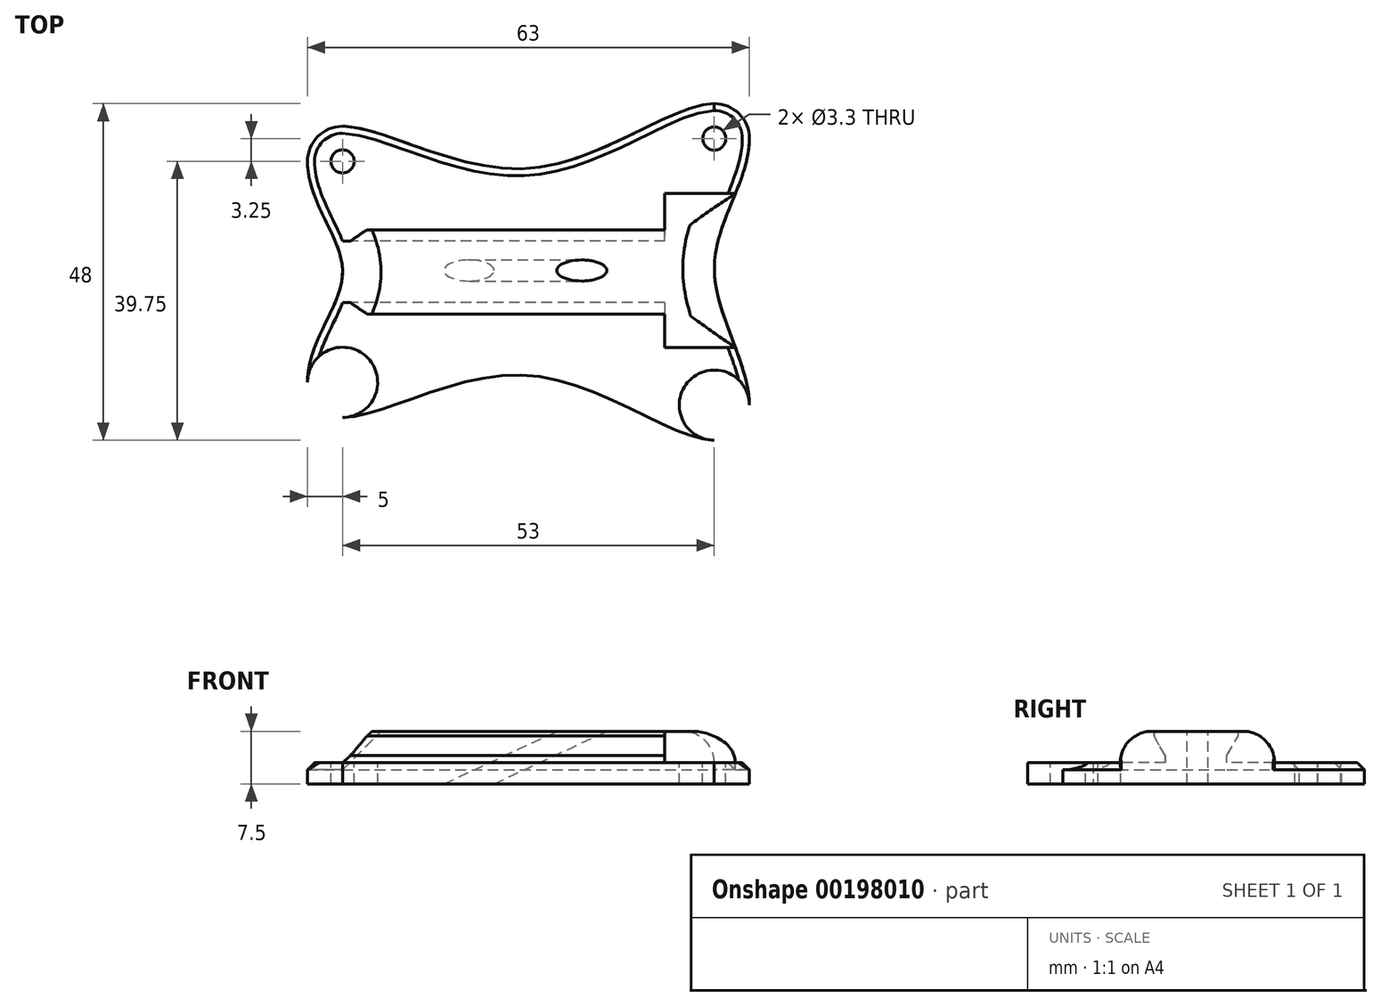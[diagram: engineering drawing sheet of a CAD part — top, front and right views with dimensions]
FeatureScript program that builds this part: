
annotation { "Feature Type Name" : "Feature", "Feature Type Description" : "" }
export const myFeature = defineFeature(function(context is Context, id is Id, definition is map)
    precondition{}
    {
        {
            var Q0;
            Q0=qCreatedBy(makeId("Top.planeOp"),FACE);
            var sketch = newSketch(context, id + "F0", { "sketchPlane" : qUnion([Q0])});
            skCircle(sketch, "E0", {"center": v(-26.5, 15.75) * mm, "radius": 5 * mm});
            skCircle(sketch, "E1", {"center": v(26.5, 19) * mm, "radius": 5 * mm});
            skFitSpline(sketch, "E2", {"points": [v(-26.5, 20.75) * mm, v(0, 14.75) * mm, v(26.5, 24) * mm], "startDerivative": vector(36.3, 0) * mm, "endDerivative": vector(35.7, 0) * mm});
            skCircle(sketch, "E3.MirrorC", {"center": v(-26.5, -15.75) * mm, "radius": 5 * mm});
            skCircle(sketch, "E4.MirrorC", {"center": v(26.5, -19) * mm, "radius": 5 * mm});
            skFitSpline(sketch, "E5", {"points": [v(-31.5, 15.75) * mm, v(-26.5, 0) * mm, v(-31.5, -15.75) * mm], "startDerivative": vector(0, -36) * mm, "endDerivative": vector(0, -36) * mm});
            skFitSpline(sketch, "E6", {"points": [v(31.5, 19) * mm, v(26.5, 0.68) * mm, v(31.5, -19) * mm], "startDerivative": vector(0, -36.61) * mm, "endDerivative": vector(0, -35.4) * mm});
            skFitSpline(sketch, "E7.MirrorCS", {"points": [v(-26.5, -20.75) * mm, v(0, -14.75) * mm, v(26.5, -24) * mm], "startDerivative": vector(36.3, 0) * mm, "endDerivative": vector(35.7, 0) * mm});
            skLineSegment(sketch, "E8", {"start": v(-31.5, 15.75) * mm, "end": v(-31.5, -15.75) * mm});
            skLineSegment(sketch, "E9", {"start": v(31.5, -19) * mm, "end": v(31.5, 19) * mm});
            skSolve(sketch);
        }
        {
            var Q0;
            {var subQ0=sQuery(id+"F0.wireOp",EDGE,"E0");var subQ1=makeQuery(id+"F0.imprint","INTERSECT",VERTEX,{"derivedFrom":[subQ0,sQuery(id+"F0.wireOp",EDGE,"E2")]});Q0=makeQuery(id+"F0.imprint","IMPRINT",FACE,{"disambiguationData":[TD([[makeQuery(id+"F0.imprint","IMPRINT",EDGE,{"disambiguationData":[TD([[subQ1,-1.0]])],"derivedFrom":subQ0}),1.0]])]});}
            var Q1;
            {var subQ3=sQuery(id+"F0.wireOp",EDGE,"E2");Q1=makeQuery(id+"F0.imprint","IMPRINT",FACE,{"disambiguationData":[TD([[makeQuery(id+"F0.imprint","IMPRINT",EDGE,{"derivedFrom":subQ3}),-1.0]])]});}
            var Q2;
            {var subQ0=sQuery(id+"F0.wireOp",EDGE,"E1");var subQ1=makeQuery(id+"F0.imprint","INTERSECT",VERTEX,{"derivedFrom":[subQ0,sQuery(id+"F0.wireOp",EDGE,"E2")]});Q2=makeQuery(id+"F0.imprint","IMPRINT",FACE,{"disambiguationData":[TD([[makeQuery(id+"F0.imprint","IMPRINT",EDGE,{"disambiguationData":[TD([[subQ1,-1.0]])],"derivedFrom":subQ0}),1.0]])]});}
            var Q3;
            {var subQ0=sQuery(id+"F0.wireOp",EDGE,"E4.MirrorC");var subQ1=makeQuery(id+"F0.imprint","INTERSECT",VERTEX,{"derivedFrom":[sQuery(id+"F0.wireOp",EDGE,"a44881bb-c97c-418e-afc0-beb98dd81ed20.MirrorCS"),subQ0]});Q3=makeQuery(id+"F0.imprint","IMPRINT",FACE,{"disambiguationData":[TD([[makeQuery(id+"F0.imprint","IMPRINT",EDGE,{"disambiguationData":[TD([[subQ1,-1.0]])],"derivedFrom":subQ0}),-1.0]])]});}
            var Q4;
            {var subQ0=sQuery(id+"F0.wireOp",EDGE,"E3.MirrorC");var subQ1=makeQuery(id+"F0.imprint","INTERSECT",VERTEX,{"derivedFrom":[subQ0,sQuery(id+"F0.wireOp",EDGE,"a44881bb-c97c-418e-afc0-beb98dd81ed20.MirrorCS")]});Q4=makeQuery(id+"F0.imprint","IMPRINT",FACE,{"disambiguationData":[TD([[makeQuery(id+"F0.imprint","IMPRINT",EDGE,{"disambiguationData":[TD([[subQ1,-1.0]])],"derivedFrom":subQ0}),-1.0]])]});}
            extrude(context, id + "F1", {"entities" : qUnion([Q0, Q1, Q2, Q3, Q4]), "oppositeDirection" : true, "depth" : 3 * mm});
        }
        {
            var Q0;
            Q0=sQuery(id+"F0.wireOp",VERTEX,"E0.center");
            var Q1;
            Q1=sQuery(id+"F0.wireOp",VERTEX,"E3.MirrorC.center");
            var Q2;
            Q2=sQuery(id+"F0.wireOp",VERTEX,"E1.center");
            var Q3;
            Q3=sQuery(id+"F0.wireOp",VERTEX,"E4.MirrorC.center");
            var Q4;
            Q4=makeQuery(id+"F1.opExtrude","SWEPT_BODY",BODY,{"disambiguationData":[OSD([sQuery(id+"F0.wireOp",EDGE,"E0"),sQuery(id+"F0.wireOp",EDGE,"E1"),sQuery(id+"F0.wireOp",EDGE,"E2"),sQuery(id+"F0.wireOp",EDGE,"E3.MirrorC"),sQuery(id+"F0.wireOp",EDGE,"E4.MirrorC"),sQuery(id+"F0.wireOp",EDGE,"E5"),sQuery(id+"F0.wireOp",EDGE,"E6"),sQuery(id+"F0.wireOp",EDGE,"E7.MirrorCS")])]});
            hole(context, id + "F2", {"style" : HoleStyle.SIMPLE, "endStyle" : HoleEndStyle.THROUGH, "holeDiameter" : 3.3 * mm, "locations" : qUnion([Q0, Q1, Q2, Q3]), "scope" : qUnion([Q4]), "isTappedThrough" : true});
        }
        {
            var Q0;
            Q0=sQuery(id+"F0.wireOp",EDGE,"E8");
            var Q1;
            {var subQ3=sQuery(id+"F0.wireOp",EDGE,"E2");Q1=makeQuery(id+"F0.imprint","IMPRINT",FACE,{"disambiguationData":[TD([[makeQuery(id+"F0.imprint","IMPRINT",EDGE,{"derivedFrom":subQ3}),-1.0]])]});}
            cPlane(context, id + "F3", {"entities" : qUnion([Q0, Q1]), "cplaneType" : CPlaneType.LINE_ANGLE, "offset" : 25 * mm, "angle" : 90 * degree, "width" : 150 * mm, "height" : 150 * mm});
        }
        {
            var Q0;
            Q0=qCreatedBy(id+"F3.planeOp",FACE);
            var sketch = newSketch(context, id + "F4", { "sketchPlane" : qUnion([Q0])});
            skLineSegment(sketch, "E10.bottom", {"start": v(6.4, 4.5) * mm, "end": v(-6.4, 4.5) * mm});
            skLineSegment(sketch, "E10.top", {"start": v(6.4, 0) * mm, "end": v(-6.4, 0) * mm});
            skLineSegment(sketch, "E10.left", {"start": v(6.4, 4.5) * mm, "end": v(6.4, 0) * mm});
            skLineSegment(sketch, "E10.right", {"start": v(-6.4, 4.5) * mm, "end": v(-6.4, 0) * mm});
            skLineSegment(sketch, "E11", {"start": v(6.4, 4.5) * mm, "end": v(4.4, 1.04) * mm});
            skLineSegment(sketch, "E12", {"start": v(4.4, 1.04) * mm, "end": v(4.4, 0) * mm});
            skLineSegment(sketch, "E13", {"start": v(0, 4.5) * mm, "end": v(0, 0) * mm, "construction": true});
            skLineSegment(sketch, "E14.MirrorCS", {"start": v(-6.4, 4.5) * mm, "end": v(-4.4, 1.04) * mm});
            skLineSegment(sketch, "E15.MirrorCS", {"start": v(-4.4, 1.04) * mm, "end": v(-4.4, 0) * mm});
            skLineSegment(sketch, "E16", {"start": v(6, 4.5) * mm, "end": v(6, 3.8) * mm});
            skLineSegment(sketch, "E17.MirrorCS", {"start": v(-6, 4.5) * mm, "end": v(-6, 3.8) * mm});
            skSolve(sketch);
        }
        {
            var Q0;
            {var subQ0=sQuery(id+"F4.wireOp",EDGE,"E12");Q0=makeQuery(id+"F4.imprint","IMPRINT",FACE,{"disambiguationData":[TD([[makeQuery(id+"F4.imprint","IMPRINT",EDGE,{"derivedFrom":subQ0}),-1.0]])]});}
            var Q1;
            Q1=makeQuery(id+"F1.opExtrude","SWEPT_BODY",BODY,{"disambiguationData":[OSD([sQuery(id+"F0.wireOp",EDGE,"E0"),sQuery(id+"F0.wireOp",EDGE,"E1"),sQuery(id+"F0.wireOp",EDGE,"E2"),sQuery(id+"F0.wireOp",EDGE,"E3.MirrorC"),sQuery(id+"F0.wireOp",EDGE,"E4.MirrorC"),sQuery(id+"F0.wireOp",EDGE,"E5"),sQuery(id+"F0.wireOp",EDGE,"E6"),sQuery(id+"F0.wireOp",EDGE,"E7.MirrorCS")])]});
            extrude(context, id + "F5", {"entities" : qUnion([Q0]), "operationType" : NewBodyOperationType.ADD, "endBoundEntityBody" : qUnion([Q1]), "depth" : 60.95 * mm});
        }
        {
            var Q0;
            Q0=makeQuery(id+"F5.opExtrude","SWEPT_FACE",FACE,{"disambiguationData":[OSD([sQuery(id+"F4.wireOp",EDGE,"E10.bottom")])]});
            var sketch = newSketch(context, id + "F6", { "sketchPlane" : qUnion([Q0])});
            skLineSegment(sketch, "E18.bottom", {"start": v(19.45, 11.2) * mm, "end": v(29.45, 11.2) * mm});
            skLineSegment(sketch, "E18.top", {"start": v(19.45, -10.8) * mm, "end": v(29.45, -10.8) * mm});
            skLineSegment(sketch, "E18.left", {"start": v(19.45, 11.2) * mm, "end": v(19.45, -10.8) * mm});
            skLineSegment(sketch, "E18.right", {"start": v(29.45, 11.2) * mm, "end": v(29.45, -10.8) * mm});
            skSolve(sketch);
        }
        {
            var Q0;
            Q0=sQuery(id+"F6.wireOp",EDGE,"E18.left");
            var Q1;
            {var subQ1=sQuery(id+"F4.wireOp",EDGE,"E10.bottom");var subQ6=makeQuery(id+"F5.opExtrude","CAP_EDGE",EDGE,{"disambiguationData":[OSD([subQ1])],"isStart":true});Q1=makeQuery(id+"F6.imprint","IMPRINT",FACE,{"disambiguationData":[TD([[makeQuery(id+"F6.imprint","IMPRINT",EDGE,{"derivedFrom":subQ6}),1.0]])]});}
            cPlane(context, id + "F7", {"entities" : qUnion([Q0, Q1]), "cplaneType" : CPlaneType.LINE_ANGLE, "offset" : 25 * mm, "angle" : 115 * degree, "width" : 150 * mm, "height" : 150 * mm});
        }
        {
            var Q0;
            {var subQ0=sQuery(id+"F6.wireOp",EDGE,"E18.top");Q0=makeQuery(id+"F6.imprint","IMPRINT",FACE,{"disambiguationData":[TD([[makeQuery(id+"F6.imprint","IMPRINT",EDGE,{"derivedFrom":subQ0}),1.0]])]});}
            var Q1;
            {var subQ0=sQuery(id+"F6.wireOp",EDGE,"E18.left");var subQ1=sQuery(id+"F4.wireOp",EDGE,"E10.bottom");var subQ2=makeQuery(id+"F5.opExtrude","SWEPT_EDGE",EDGE,{"disambiguationData":[OSD([subQ1,sQuery(id+"F4.wireOp",EDGE,"E10.left"),sQuery(id+"F4.wireOp",EDGE,"E11")])]});var subQ3=makeQuery(id+"F6.imprint","INTERSECT",VERTEX,{"derivedFrom":[subQ2,subQ0]});Q1=makeQuery(id+"F6.imprint","IMPRINT",FACE,{"disambiguationData":[TD([[makeQuery(id+"F6.imprint","IMPRINT",EDGE,{"disambiguationData":[TD([[subQ3,-1.0]])],"derivedFrom":subQ0}),1.0]])]});}
            var Q2;
            {var subQ0=sQuery(id+"F6.wireOp",EDGE,"E18.bottom");Q2=makeQuery(id+"F6.imprint","IMPRINT",FACE,{"disambiguationData":[TD([[makeQuery(id+"F6.imprint","IMPRINT",EDGE,{"derivedFrom":subQ0}),-1.0]])]});}
            extrude(context, id + "F8", {"entities" : qUnion([Q0, Q1, Q2]), "operationType" : NewBodyOperationType.ADD, "oppositeDirection" : true, "depth" : 4.5 * mm});
        }
        {
            var Q0;
            Q0=makeQuery(id+"F0.imprint","IMPRINT",FACE,{"disambiguationData":[TD([[makeQuery(id+"F0.imprint","IMPRINT",EDGE,{"derivedFrom":sQuery(id+"F0.wireOp",EDGE,"E6")}),1.0]])]});
            var Q1;
            Q1=makeQuery(id+"F0.imprint","IMPRINT",FACE,{"disambiguationData":[TD([[makeQuery(id+"F0.imprint","IMPRINT",EDGE,{"derivedFrom":sQuery(id+"F0.wireOp",EDGE,"E5")}),-1.0]])]});
            extrude(context, id + "F9", {"entities" : qUnion([Q0, Q1]), "operationType" : NewBodyOperationType.REMOVE, "endBound" : BoundingType.THROUGH_ALL, "depth" : 25 * mm});
        }
        {
            var Q0;
            Q0=makeQuery(id+"F8.opExtrude","CAP_EDGE",EDGE,{"disambiguationData":[OSD([sQuery(id+"F6.wireOp",EDGE,"E18.top")])],"isStart":true});
            var Q1;
            Q1=makeQuery(id+"F9.boolean.opBoolean","INTERSECT",EDGE,{"derivedFrom":[makeQuery(id+"F8.boolean.opBoolean","MERGE",FACE,{"derivedFrom":[makeQuery(id+"F5.opExtrude","SWEPT_FACE",FACE,{"disambiguationData":[OSD([sQuery(id+"F4.wireOp",EDGE,"E10.bottom")])]}),makeQuery(id+"F8.opExtrude","CAP_FACE",FACE,{"disambiguationData":[OSD([sQuery(id+"F6.wireOp",EDGE,"E18.bottom"),sQuery(id+"F6.wireOp",EDGE,"E18.top"),sQuery(id+"F6.wireOp",EDGE,"E18.left"),sQuery(id+"F6.wireOp",EDGE,"E18.right")])],"isStart":true})]}),makeQuery(id+"F9.opExtrude","SWEPT_FACE",FACE,{"disambiguationData":[OSD([sQuery(id+"F0.wireOp",EDGE,"E6")])]})]});
            var Q2;
            Q2=makeQuery(id+"F8.opExtrude","CAP_EDGE",EDGE,{"disambiguationData":[OSD([sQuery(id+"F6.wireOp",EDGE,"E18.bottom")])],"isStart":true});
            fillet(context, id + "F10", {"entities" : qUnion([Q0, Q1, Q2]), "radius" : 4.5 * mm, "tangentPropagation" : true, "allowEdgeOverflow" : false});
        }
        {
            var Q0;
            {var subQ0=sQuery(id+"F0.wireOp",EDGE,"E6");var subQ1=sQuery(id+"F0.wireOp",EDGE,"E1");Q0=makeQuery(id+"F8.boolean.opBoolean","SPLIT",EDGE,{"derivedFrom":makeQuery(id+"F5.boolean.opBoolean","SPLIT",EDGE,{"disambiguationData":[TD([makeQuery(id+"F1.opExtrude","CAP_FACE",FACE,{"disambiguationData":[OSD([sQuery(id+"F0.wireOp",EDGE,"E0"),subQ1,sQuery(id+"F0.wireOp",EDGE,"E2"),sQuery(id+"F0.wireOp",EDGE,"E3.MirrorC"),sQuery(id+"F0.wireOp",EDGE,"E4.MirrorC"),sQuery(id+"F0.wireOp",EDGE,"E5"),subQ0,sQuery(id+"F0.wireOp",EDGE,"E7.MirrorCS")])],"isStart":true}),makeQuery(id+"F1.opExtrude","SWEPT_FACE",FACE,{"disambiguationData":[OSD([subQ1])]}),makeQuery(id+"F1.opExtrude","SWEPT_FACE",FACE,{"disambiguationData":[OSD([subQ0])]}),makeQuery(id+"F5.opExtrude","SWEPT_FACE",FACE,{"disambiguationData":[OSD([sQuery(id+"F4.wireOp",EDGE,"E10.top")])]}),makeQuery(id+"F5.opExtrude","SWEPT_FACE",FACE,{"disambiguationData":[OSD([sQuery(id+"F4.wireOp",EDGE,"E12")])]})])],"derivedFrom":makeQuery(id+"F1.opExtrude","CAP_EDGE",EDGE,{"disambiguationData":[OSD([subQ0])],"isStart":true})})});}
            var Q1;
            {var subQ0=sQuery(id+"F0.wireOp",EDGE,"E6");var subQ1=sQuery(id+"F0.wireOp",EDGE,"E4.MirrorC");Q1=makeQuery(id+"F8.boolean.opBoolean","SPLIT",EDGE,{"derivedFrom":makeQuery(id+"F5.boolean.opBoolean","SPLIT",EDGE,{"disambiguationData":[TD([makeQuery(id+"F1.opExtrude","CAP_FACE",FACE,{"disambiguationData":[OSD([sQuery(id+"F0.wireOp",EDGE,"E0"),sQuery(id+"F0.wireOp",EDGE,"E1"),sQuery(id+"F0.wireOp",EDGE,"E2"),sQuery(id+"F0.wireOp",EDGE,"E3.MirrorC"),subQ1,sQuery(id+"F0.wireOp",EDGE,"E5"),subQ0,sQuery(id+"F0.wireOp",EDGE,"E7.MirrorCS")])],"isStart":true}),makeQuery(id+"F1.opExtrude","SWEPT_FACE",FACE,{"disambiguationData":[OSD([subQ1])]}),makeQuery(id+"F1.opExtrude","SWEPT_FACE",FACE,{"disambiguationData":[OSD([subQ0])]}),makeQuery(id+"F5.opExtrude","SWEPT_FACE",FACE,{"disambiguationData":[OSD([sQuery(id+"F4.wireOp",EDGE,"E10.top")])]}),makeQuery(id+"F5.opExtrude","SWEPT_FACE",FACE,{"disambiguationData":[OSD([sQuery(id+"F4.wireOp",EDGE,"E15.MirrorCS")])]})])],"derivedFrom":makeQuery(id+"F1.opExtrude","CAP_EDGE",EDGE,{"disambiguationData":[OSD([subQ0])],"isStart":true})})});}
            chamfer(context, id + "F11", {"entities" : qUnion([Q0, Q1]), "width" : 1 * mm, "tangentPropagation" : true});
        }
        {
            var Q0;
            Q0=makeQuery(id+"F9.boolean.opBoolean","INTERSECT",EDGE,{"derivedFrom":[makeQuery(id+"F8.boolean.opBoolean","MERGE",FACE,{"derivedFrom":[makeQuery(id+"F5.opExtrude","SWEPT_FACE",FACE,{"disambiguationData":[OSD([sQuery(id+"F4.wireOp",EDGE,"E10.bottom")])]}),makeQuery(id+"F8.opExtrude","CAP_FACE",FACE,{"disambiguationData":[OSD([sQuery(id+"F6.wireOp",EDGE,"E18.bottom"),sQuery(id+"F6.wireOp",EDGE,"E18.top"),sQuery(id+"F6.wireOp",EDGE,"E18.left"),sQuery(id+"F6.wireOp",EDGE,"E18.right")])],"isStart":true})]}),makeQuery(id+"F9.opExtrude","SWEPT_FACE",FACE,{"disambiguationData":[OSD([sQuery(id+"F0.wireOp",EDGE,"E5")])]})]});
            chamfer(context, id + "F12", {"entities" : qUnion([Q0]), "width" : 5.5 * mm, "tangentPropagation" : true});
        }
        {
            var Q0;
            Q0=qCreatedBy(id+"F7.planeOp",FACE);
            var sketch = newSketch(context, id + "F13", { "sketchPlane" : qUnion([Q0])});
            skLineSegment(sketch, "E19", {"start": v(-7.26, 0.86) * mm, "end": v(7.22, 0.86) * mm, "construction": true});
            skPoint(sketch, "E20", {"position": v(0.2, 0.86) * mm});
            skSolve(sketch);
        }
        {
            var Q0;
            Q0=sQuery(id+"F13.wireOp",VERTEX,"E20");
            var Q1;
            Q1=makeQuery(id+"F1.opExtrude","SWEPT_BODY",BODY,{"disambiguationData":[OSD([sQuery(id+"F0.wireOp",EDGE,"E0"),sQuery(id+"F0.wireOp",EDGE,"E1"),sQuery(id+"F0.wireOp",EDGE,"E2"),sQuery(id+"F0.wireOp",EDGE,"E3.MirrorC"),sQuery(id+"F0.wireOp",EDGE,"E4.MirrorC"),sQuery(id+"F0.wireOp",EDGE,"E5"),sQuery(id+"F0.wireOp",EDGE,"E6"),sQuery(id+"F0.wireOp",EDGE,"E7.MirrorCS")])]});
            hole(context, id + "F14", {"style" : HoleStyle.SIMPLE, "endStyle" : HoleEndStyle.THROUGH, "holeDiameter" : 3 * mm, "locations" : qUnion([Q0]), "scope" : qUnion([Q1]), "isTappedThrough" : true});
        }
    });
